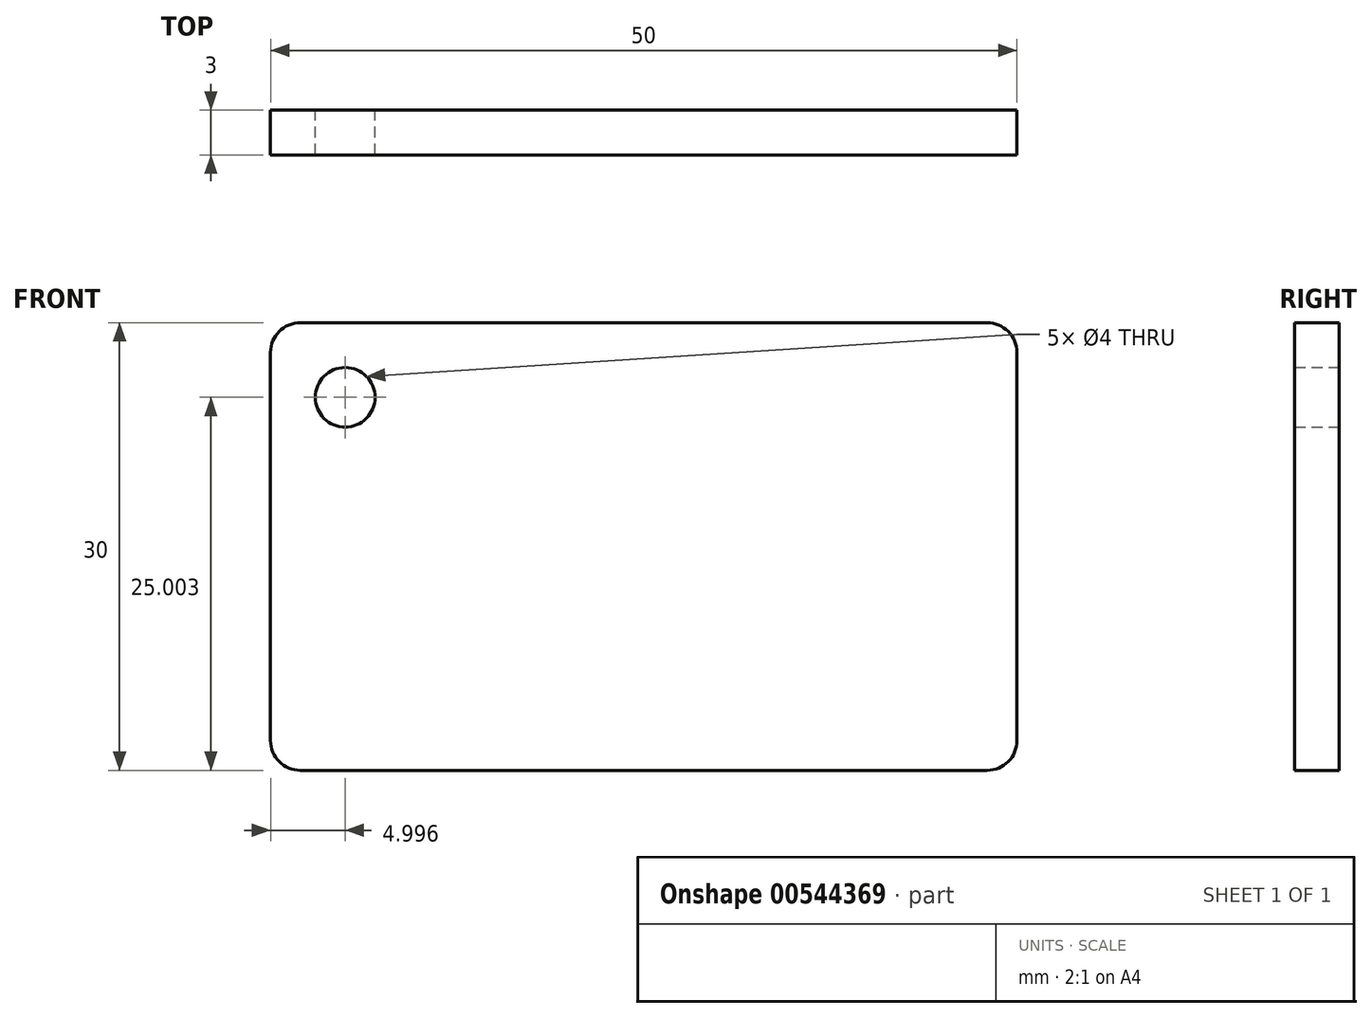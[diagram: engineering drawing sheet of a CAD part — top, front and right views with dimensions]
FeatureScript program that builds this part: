
annotation { "Feature Type Name" : "Feature", "Feature Type Description" : "" }
export const myFeature = defineFeature(function(context is Context, id is Id, definition is map)
    precondition{}
    {
        {
            var Q0;
            Q0=qCreatedBy(makeId("Front.planeOp"),FACE);
            var sketch = newSketch(context, id + "F0", { "sketchPlane" : qUnion([Q0])});
            skLineSegment(sketch, "E0.bottom", {"start": v(-48.92, 11.46) * mm, "end": v(1.08, 11.46) * mm});
            skLineSegment(sketch, "E0.top", {"start": v(-48.92, -18.54) * mm, "end": v(1.08, -18.54) * mm});
            skLineSegment(sketch, "E0.left", {"start": v(-48.92, 11.46) * mm, "end": v(-48.92, -18.54) * mm});
            skLineSegment(sketch, "E0.right", {"start": v(1.08, 11.46) * mm, "end": v(1.08, -18.54) * mm});
            skCircle(sketch, "E1", {"center": v(-43.92, 6.46) * mm, "radius": 2 * mm});
            skSolve(sketch);
        }
        {
            var Q0;
            Q0 = qSketchRegion(id + "F0", true);
            extrude(context, id + "F1", {"entities" : qUnion([Q0]), "depth" : 3 * mm, "offsetDistance" : 25.4 * mm});
        }
        {
            var Q0;
            Q0=makeQuery(id+"F1.opExtrude","SWEPT_EDGE",EDGE,{"disambiguationData":[OSD([sQuery(id+"F0.wireOp",EDGE,"E0.top"),sQuery(id+"F0.wireOp",EDGE,"E0.left")])]});
            var Q1;
            Q1=makeQuery(id+"F1.opExtrude","SWEPT_EDGE",EDGE,{"disambiguationData":[OSD([sQuery(id+"F0.wireOp",EDGE,"E0.top"),sQuery(id+"F0.wireOp",EDGE,"E0.right")])]});
            var Q2;
            Q2=makeQuery(id+"F1.opExtrude","SWEPT_EDGE",EDGE,{"disambiguationData":[OSD([sQuery(id+"F0.wireOp",EDGE,"E0.bottom"),sQuery(id+"F0.wireOp",EDGE,"E0.right")])]});
            var Q3;
            Q3=makeQuery(id+"F1.opExtrude","SWEPT_EDGE",EDGE,{"disambiguationData":[OSD([sQuery(id+"F0.wireOp",EDGE,"E0.bottom"),sQuery(id+"F0.wireOp",EDGE,"E0.left")])]});
            fillet(context, id + "F2", {"entities" : qUnion([Q0, Q1, Q2, Q3]), "radius" : 2 * mm, "tangentPropagation" : true, "allowEdgeOverflow" : false});
        }
    });
